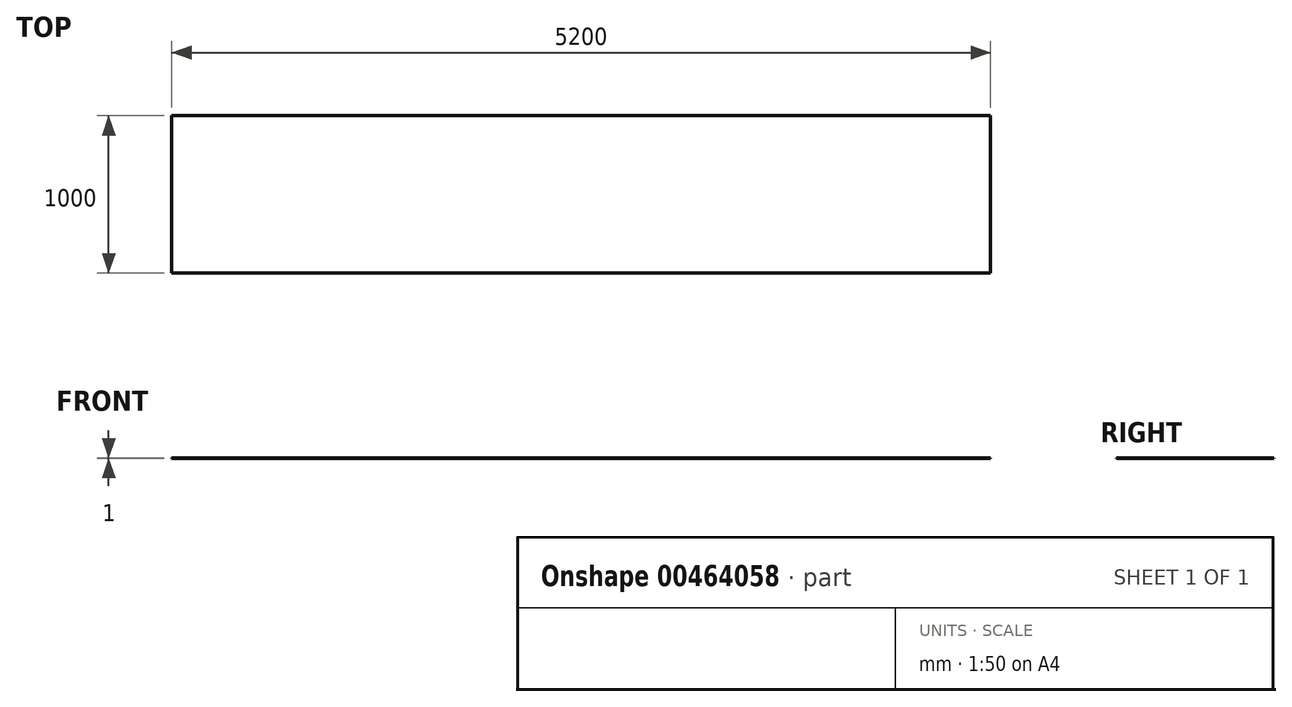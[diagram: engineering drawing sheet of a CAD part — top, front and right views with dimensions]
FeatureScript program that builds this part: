
annotation { "Feature Type Name" : "Feature", "Feature Type Description" : "" }
export const myFeature = defineFeature(function(context is Context, id is Id, definition is map)
    precondition{}
    {
        {
            var Q0;
            Q0=qCreatedBy(makeId("Top.planeOp"),FACE);
            var sketch = newSketch(context, id + "F0", { "sketchPlane" : qUnion([Q0])});
            skLineSegment(sketch, "E0.bottom", {"start": v(0, 0) * mm, "end": v(-5200, 0) * mm});
            skLineSegment(sketch, "E0.top", {"start": v(0, -1000) * mm, "end": v(-5200, -1000) * mm});
            skLineSegment(sketch, "E0.left", {"start": v(0, 0) * mm, "end": v(0, -1000) * mm});
            skLineSegment(sketch, "E0.right", {"start": v(-5200, 0) * mm, "end": v(-5200, -1000) * mm});
            skSolve(sketch);
        }
        {
            var Q0;
            Q0=qSketchRegion(id+"F0",true);
            extrude(context, id + "F1", {"entities" : qUnion([Q0]), "depth" : 1 * mm});
        }
    });
